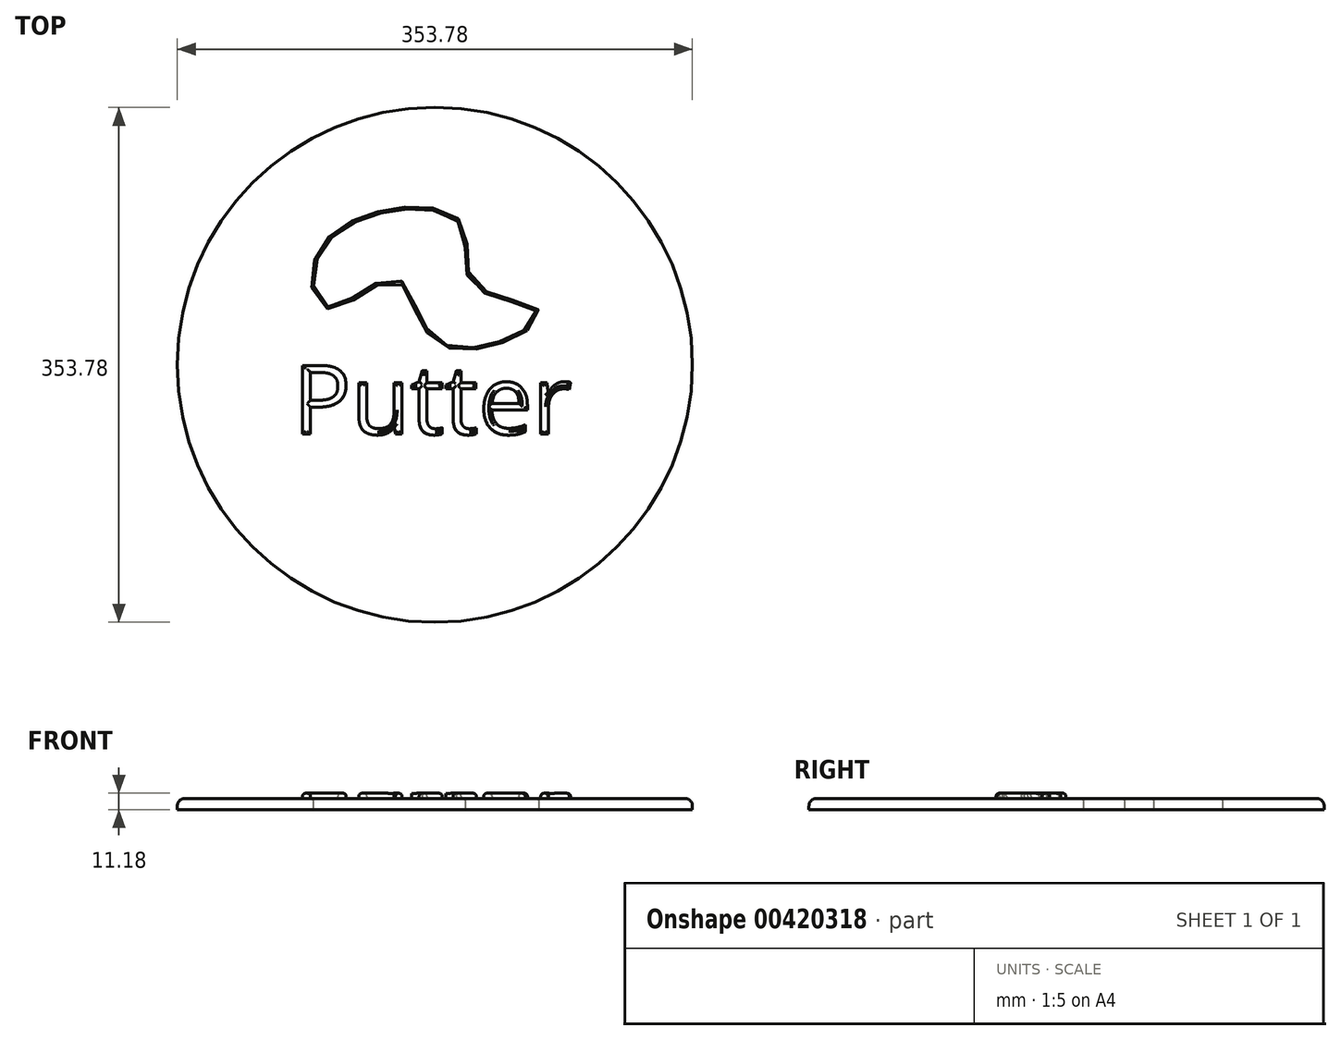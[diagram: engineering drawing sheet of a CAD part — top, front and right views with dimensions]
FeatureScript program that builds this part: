
annotation { "Feature Type Name" : "Feature", "Feature Type Description" : "" }
export const myFeature = defineFeature(function(context is Context, id is Id, definition is map)
    precondition{}
    {
        {
            var Q0;
            Q0=qCreatedBy(makeId("Top.planeOp"),FACE);
            var sketch = newSketch(context, id + "F0", { "sketchPlane" : qUnion([Q0])});
            skCircle(sketch, "E0", {"center": v(0, 0) * mm, "radius": 176.9 * mm});
            skSolve(sketch);
        }
        {
            var Q0;
            Q0 = qSketchRegion(id + "F0", true);
            extrude(context, id + "F1", {"entities" : qUnion([Q0]), "oppositeDirection" : true, "depth" : 7.62 * mm});
        }
        {
            var Q0;
            Q0=qCreatedBy(makeId("Top.planeOp"),FACE);
            var sketch = newSketch(context, id + "F2", { "sketchPlane" : qUnion([Q0])});
            skText(sketch, "E1", { "text": "Putter", "fontName": "OpenSans-Regular.ttf"});
            const initialGuessF2  = {"E1": [-0.09742, -0.04769, 1, 0, 0.04769]};
            skSetInitialGuess(sketch, initialGuessF2);
            skSolve(sketch);
        }
        {
            var Q0;
            Q0 = qSketchRegion(id + "F2", true);
            extrude(context, id + "F3", {"entities" : qUnion([Q0]), "operationType" : NewBodyOperationType.ADD, "depth" : 3.56 * mm});
        }
        {
            var Q0;
            {var subQ0=sQuery(id+"F0.wireOp",EDGE,"E0");Q0=makeQuery(id+"F3.boolean.opBoolean","SPLIT",FACE,{"disambiguationData":[TD([makeQuery(id+"F1.opExtrude","SWEPT_FACE",FACE,{"disambiguationData":[OSD([subQ0])]})])],"derivedFrom":makeQuery(id+"F1.opExtrude","CAP_FACE",FACE,{"disambiguationData":[OSD([subQ0])],"isStart":true})});}
            var sketch = newSketch(context, id + "F4", { "sketchPlane" : qUnion([Q0])});
            skSolve(sketch);
        }
        {
            var Q0;
            Q0=makeQuery(id+"F1.opExtrude","CAP_EDGE",EDGE,{"disambiguationData":[OSD([sQuery(id+"F0.wireOp",EDGE,"E0")])],"isStart":true});
            fillet(context, id + "F5", {"entities" : qUnion([Q0]), "radius" : 5.08 * mm, "tangentPropagation" : true, "allowEdgeOverflow" : false});
        }
        {
            var Q0;
            Q0=makeQuery(id+"F3.opExtrude","CAP_FACE",FACE,{"disambiguationData":[OSD([sQuery(id+"F2.wireOp",EDGE,"E1.sketch_text.stroke-0"),sQuery(id+"F2.wireOp",EDGE,"E1.sketch_text.stroke-1"),sQuery(id+"F2.wireOp",EDGE,"E1.sketch_text.stroke-2"),sQuery(id+"F2.wireOp",EDGE,"E1.sketch_text.stroke-3"),sQuery(id+"F2.wireOp",EDGE,"E1.sketch_text.stroke-4"),sQuery(id+"F2.wireOp",EDGE,"E1.sketch_text.stroke-5"),sQuery(id+"F2.wireOp",EDGE,"E1.sketch_text.stroke-6"),sQuery(id+"F2.wireOp",EDGE,"E1.sketch_text.stroke-7"),sQuery(id+"F2.wireOp",EDGE,"E1.sketch_text.stroke-8"),sQuery(id+"F2.wireOp",EDGE,"E1.sketch_text.stroke-9"),sQuery(id+"F2.wireOp",EDGE,"E1.sketch_text.stroke-10"),sQuery(id+"F2.wireOp",EDGE,"E1.sketch_text.stroke-11"),sQuery(id+"F2.wireOp",EDGE,"E1.sketch_text.stroke-12"),sQuery(id+"F2.wireOp",EDGE,"E1.sketch_text.stroke-13"),sQuery(id+"F2.wireOp",EDGE,"E1.sketch_text.stroke-14")])],"isStart":false});
            var Q1;
            Q1=makeQuery(id+"F3.opExtrude","CAP_FACE",FACE,{"disambiguationData":[OSD([sQuery(id+"F2.wireOp",EDGE,"E1.sketch_text.stroke-15"),sQuery(id+"F2.wireOp",EDGE,"E1.sketch_text.stroke-16"),sQuery(id+"F2.wireOp",EDGE,"E1.sketch_text.stroke-17"),sQuery(id+"F2.wireOp",EDGE,"E1.sketch_text.stroke-18"),sQuery(id+"F2.wireOp",EDGE,"E1.sketch_text.stroke-19"),sQuery(id+"F2.wireOp",EDGE,"E1.sketch_text.stroke-20"),sQuery(id+"F2.wireOp",EDGE,"E1.sketch_text.stroke-21"),sQuery(id+"F2.wireOp",EDGE,"E1.sketch_text.stroke-22"),sQuery(id+"F2.wireOp",EDGE,"E1.sketch_text.stroke-23"),sQuery(id+"F2.wireOp",EDGE,"E1.sketch_text.stroke-24"),sQuery(id+"F2.wireOp",EDGE,"E1.sketch_text.stroke-25"),sQuery(id+"F2.wireOp",EDGE,"E1.sketch_text.stroke-26"),sQuery(id+"F2.wireOp",EDGE,"E1.sketch_text.stroke-27"),sQuery(id+"F2.wireOp",EDGE,"E1.sketch_text.stroke-28"),sQuery(id+"F2.wireOp",EDGE,"E1.sketch_text.stroke-29"),sQuery(id+"F2.wireOp",EDGE,"E1.sketch_text.stroke-30"),sQuery(id+"F2.wireOp",EDGE,"E1.sketch_text.stroke-31")])],"isStart":false});
            var Q2;
            Q2=makeQuery(id+"F3.opExtrude","CAP_FACE",FACE,{"disambiguationData":[OSD([sQuery(id+"F2.wireOp",EDGE,"E1.sketch_text.stroke-32"),sQuery(id+"F2.wireOp",EDGE,"E1.sketch_text.stroke-33"),sQuery(id+"F2.wireOp",EDGE,"E1.sketch_text.stroke-34"),sQuery(id+"F2.wireOp",EDGE,"E1.sketch_text.stroke-35"),sQuery(id+"F2.wireOp",EDGE,"E1.sketch_text.stroke-36"),sQuery(id+"F2.wireOp",EDGE,"E1.sketch_text.stroke-37"),sQuery(id+"F2.wireOp",EDGE,"E1.sketch_text.stroke-38"),sQuery(id+"F2.wireOp",EDGE,"E1.sketch_text.stroke-39"),sQuery(id+"F2.wireOp",EDGE,"E1.sketch_text.stroke-40"),sQuery(id+"F2.wireOp",EDGE,"E1.sketch_text.stroke-41"),sQuery(id+"F2.wireOp",EDGE,"E1.sketch_text.stroke-42"),sQuery(id+"F2.wireOp",EDGE,"E1.sketch_text.stroke-43"),sQuery(id+"F2.wireOp",EDGE,"E1.sketch_text.stroke-44"),sQuery(id+"F2.wireOp",EDGE,"E1.sketch_text.stroke-45"),sQuery(id+"F2.wireOp",EDGE,"E1.sketch_text.stroke-46"),sQuery(id+"F2.wireOp",EDGE,"E1.sketch_text.stroke-47"),sQuery(id+"F2.wireOp",EDGE,"E1.sketch_text.stroke-48"),sQuery(id+"F2.wireOp",EDGE,"E1.sketch_text.stroke-49"),sQuery(id+"F2.wireOp",EDGE,"E1.sketch_text.stroke-50")])],"isStart":false});
            var Q3;
            Q3=makeQuery(id+"F3.opExtrude","CAP_FACE",FACE,{"disambiguationData":[OSD([sQuery(id+"F2.wireOp",EDGE,"E1.sketch_text.stroke-51"),sQuery(id+"F2.wireOp",EDGE,"E1.sketch_text.stroke-52"),sQuery(id+"F2.wireOp",EDGE,"E1.sketch_text.stroke-53"),sQuery(id+"F2.wireOp",EDGE,"E1.sketch_text.stroke-54"),sQuery(id+"F2.wireOp",EDGE,"E1.sketch_text.stroke-55"),sQuery(id+"F2.wireOp",EDGE,"E1.sketch_text.stroke-56"),sQuery(id+"F2.wireOp",EDGE,"E1.sketch_text.stroke-57"),sQuery(id+"F2.wireOp",EDGE,"E1.sketch_text.stroke-58"),sQuery(id+"F2.wireOp",EDGE,"E1.sketch_text.stroke-59"),sQuery(id+"F2.wireOp",EDGE,"E1.sketch_text.stroke-60"),sQuery(id+"F2.wireOp",EDGE,"E1.sketch_text.stroke-61"),sQuery(id+"F2.wireOp",EDGE,"E1.sketch_text.stroke-62"),sQuery(id+"F2.wireOp",EDGE,"E1.sketch_text.stroke-63"),sQuery(id+"F2.wireOp",EDGE,"E1.sketch_text.stroke-64"),sQuery(id+"F2.wireOp",EDGE,"E1.sketch_text.stroke-65"),sQuery(id+"F2.wireOp",EDGE,"E1.sketch_text.stroke-66"),sQuery(id+"F2.wireOp",EDGE,"E1.sketch_text.stroke-67"),sQuery(id+"F2.wireOp",EDGE,"E1.sketch_text.stroke-68"),sQuery(id+"F2.wireOp",EDGE,"E1.sketch_text.stroke-69")])],"isStart":false});
            var Q4;
            Q4=makeQuery(id+"F3.opExtrude","CAP_FACE",FACE,{"disambiguationData":[OSD([sQuery(id+"F2.wireOp",EDGE,"E1.sketch_text.stroke-70"),sQuery(id+"F2.wireOp",EDGE,"E1.sketch_text.stroke-71"),sQuery(id+"F2.wireOp",EDGE,"E1.sketch_text.stroke-72"),sQuery(id+"F2.wireOp",EDGE,"E1.sketch_text.stroke-73"),sQuery(id+"F2.wireOp",EDGE,"E1.sketch_text.stroke-74"),sQuery(id+"F2.wireOp",EDGE,"E1.sketch_text.stroke-75"),sQuery(id+"F2.wireOp",EDGE,"E1.sketch_text.stroke-76"),sQuery(id+"F2.wireOp",EDGE,"E1.sketch_text.stroke-77"),sQuery(id+"F2.wireOp",EDGE,"E1.sketch_text.stroke-78"),sQuery(id+"F2.wireOp",EDGE,"E1.sketch_text.stroke-79"),sQuery(id+"F2.wireOp",EDGE,"E1.sketch_text.stroke-80"),sQuery(id+"F2.wireOp",EDGE,"E1.sketch_text.stroke-81"),sQuery(id+"F2.wireOp",EDGE,"E1.sketch_text.stroke-82"),sQuery(id+"F2.wireOp",EDGE,"E1.sketch_text.stroke-83"),sQuery(id+"F2.wireOp",EDGE,"E1.sketch_text.stroke-84"),sQuery(id+"F2.wireOp",EDGE,"E1.sketch_text.stroke-85"),sQuery(id+"F2.wireOp",EDGE,"E1.sketch_text.stroke-86"),sQuery(id+"F2.wireOp",EDGE,"E1.sketch_text.stroke-87"),sQuery(id+"F2.wireOp",EDGE,"E1.sketch_text.stroke-88")])],"isStart":false});
            var Q5;
            Q5=makeQuery(id+"F3.opExtrude","CAP_FACE",FACE,{"disambiguationData":[OSD([sQuery(id+"F2.wireOp",EDGE,"E1.sketch_text.stroke-89"),sQuery(id+"F2.wireOp",EDGE,"E1.sketch_text.stroke-90"),sQuery(id+"F2.wireOp",EDGE,"E1.sketch_text.stroke-91"),sQuery(id+"F2.wireOp",EDGE,"E1.sketch_text.stroke-92"),sQuery(id+"F2.wireOp",EDGE,"E1.sketch_text.stroke-93"),sQuery(id+"F2.wireOp",EDGE,"E1.sketch_text.stroke-94"),sQuery(id+"F2.wireOp",EDGE,"E1.sketch_text.stroke-95"),sQuery(id+"F2.wireOp",EDGE,"E1.sketch_text.stroke-96"),sQuery(id+"F2.wireOp",EDGE,"E1.sketch_text.stroke-97"),sQuery(id+"F2.wireOp",EDGE,"E1.sketch_text.stroke-98"),sQuery(id+"F2.wireOp",EDGE,"E1.sketch_text.stroke-99"),sQuery(id+"F2.wireOp",EDGE,"E1.sketch_text.stroke-100"),sQuery(id+"F2.wireOp",EDGE,"E1.sketch_text.stroke-101")])],"isStart":false});
            fillet(context, id + "F6", {"entities" : qUnion([Q0, Q1, Q2, Q3, Q4, Q5]), "radius" : 2.03 * mm, "tangentPropagation" : true, "allowEdgeOverflow" : false});
        }
        {
            var Q0;
            Q0=makeQuery(id+"F4.imprint","IMPRINT",FACE,{"disambiguationData":[TD([[makeQuery(id+"F4.imprint","IMPRINT",EDGE,{"derivedFrom":makeQuery(id+"F1.opExtrude","CAP_EDGE",EDGE,{"disambiguationData":[OSD([sQuery(id+"F0.wireOp",EDGE,"E0")])],"isStart":true})}),1.0]])]});
            var sketch = newSketch(context, id + "F7", { "sketchPlane" : qUnion([Q0])});
            skFitSpline(sketch, "E2", {"points": [v(-73.49, 39.89) * mm, v(-74.19, 84.25) * mm, v(16.06, 98.52) * mm, v(25.98, 55) * mm, v(71.36, 34.62) * mm, v(6.25, 14.06) * mm, v(-26.73, 59.6) * mm, v(-73.49, 39.89) * mm]});
            skSolve(sketch);
        }
        {
            var Q0;
            Q0 = qSketchRegion(id + "F7", true);
            extrude(context, id + "F8", {"entities" : qUnion([Q0]), "operationType" : NewBodyOperationType.REMOVE, "oppositeDirection" : true, "depth" : 25.4 * mm});
        }
        {
            var Q0;
            Q0=makeQuery(id+"F8.boolean.opBoolean","COPY",FACE,{"derivedFrom":makeQuery(id+"F8.opExtrude","SWEPT_FACE",FACE,{"disambiguationData":[OSD([sQuery(id+"F7.wireOp",EDGE,"E2")])]})});
            fillet(context, id + "F9", {"entities" : qUnion([Q0]), "radius" : 1.27 * mm, "tangentPropagation" : true, "allowEdgeOverflow" : false});
        }
    });
